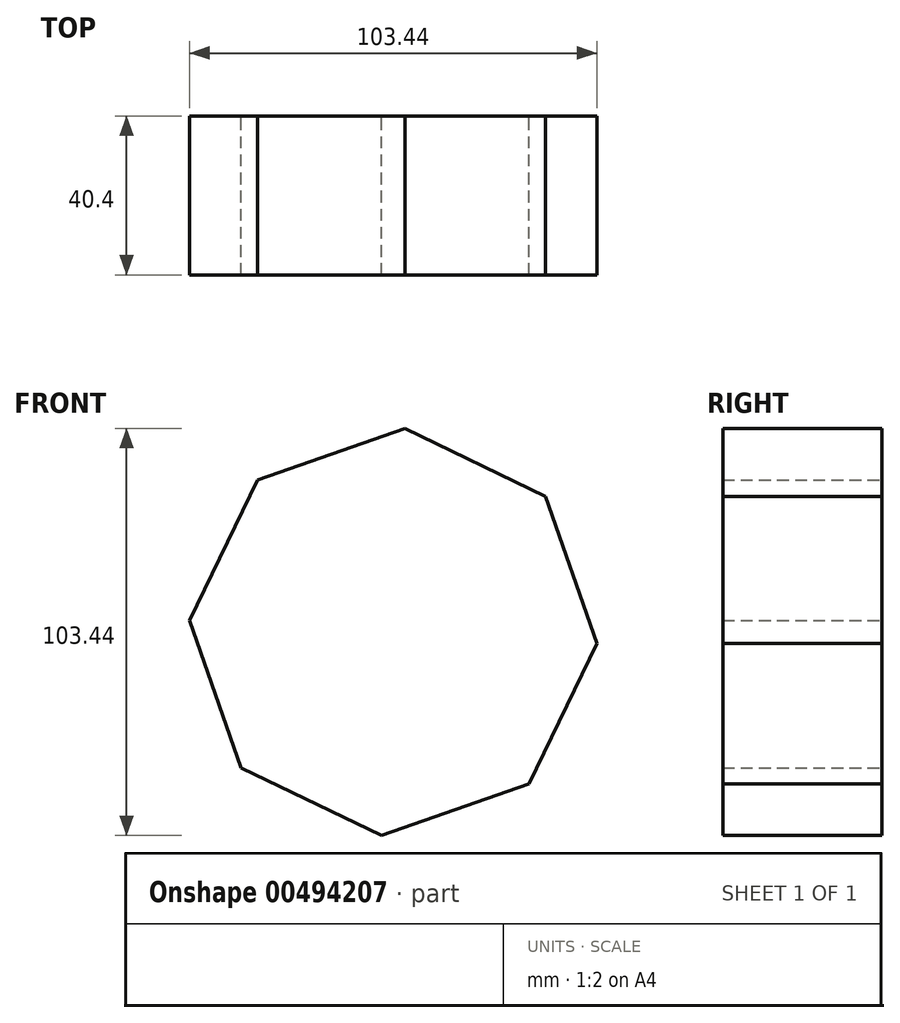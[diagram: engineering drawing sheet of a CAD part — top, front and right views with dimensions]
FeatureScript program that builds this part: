
annotation { "Feature Type Name" : "Feature", "Feature Type Description" : "" }
export const myFeature = defineFeature(function(context is Context, id is Id, definition is map)
    precondition{}
    {
        {
            var Q0;
            Q0=qCreatedBy(makeId("Front.planeOp"),FACE);
            var sketch = newSketch(context, id + "F0", { "sketchPlane" : qUnion([Q0])});
            skCircle(sketch, "E0.cCircle", {"center": v(0, 0) * mm, "radius": 47.86 * mm, "construction": true});
            skLineSegment(sketch, "E0.0", {"start": v(-34.5, 38.65) * mm, "end": v(2.94, 51.72) * mm});
            skLineSegment(sketch, "E0.1", {"start": v(2.94, 51.72) * mm, "end": v(38.65, 34.5) * mm});
            skLineSegment(sketch, "E0.2", {"start": v(38.65, 34.5) * mm, "end": v(51.72, -2.94) * mm});
            skLineSegment(sketch, "E0.3", {"start": v(51.72, -2.94) * mm, "end": v(34.5, -38.65) * mm});
            skLineSegment(sketch, "E0.4", {"start": v(34.5, -38.65) * mm, "end": v(-2.94, -51.72) * mm});
            skLineSegment(sketch, "E0.5", {"start": v(-2.94, -51.72) * mm, "end": v(-38.65, -34.5) * mm});
            skLineSegment(sketch, "E0.6", {"start": v(-38.65, -34.5) * mm, "end": v(-51.72, 2.94) * mm});
            skLineSegment(sketch, "E0.7", {"start": v(-51.72, 2.94) * mm, "end": v(-34.5, 38.65) * mm});
            skPoint(sketch, "E0.0.midPoint", {"position": v(-15.78, 45.18) * mm});
            skSolve(sketch);
        }
        {
            var Q0;
            Q0=makeQuery(id+"F0.imprint","IMPRINT",FACE,{"disambiguationData":[TD([[makeQuery(id+"F0.imprint","IMPRINT",EDGE,{"derivedFrom":sQuery(id+"F0.wireOp",EDGE,"E0.0")}),-1.0]])]});
            extrude(context, id + "F1", {"entities" : qUnion([Q0]), "depth" : 40.4 * mm});
        }
    });
